# Revit family: НЕВАТОМ_Фильтр панельный FVP, Версия 2
name_source: partatom
category: Арматура воздуховодов
revit_build: Autodesk Revit 2017 (Build: 20170118_1100(x64)
units: mm (PartAtom-declared; Revit-internal decimal feet)

## family parameters
Всегда вертикально = Нет
На основе рабочей плоскости = Нет
Общий = Нет
При загрузке вырезать с полостями = Нет
Размер круглого соединителя = Использовать диаметр
Тип детали = Вставляется

## types (8) — shared parameters
ADSK_Единица измерения = шт
ADSK_Завод-изготовитель = НЕВАТОМ
ADSK_Количество = 1
ADSK_Материал = Оцинкованная сталь
ADSK_Материал наименование = Оцинкованная сталь
L = 25 мм
Nevatom_URL = https://t.me
t = 25 мм
zero-valued in all types: ADSK_Масса

## per-type parameters (varying)
| type | ADSK_Расход воздуха |
| 500х500х25 | 1700.0 м³/ч |
| 592х592х25 | 2400.0 м³/ч |
| 592х287х25 | 1200.0 м³/ч |
| 592х490х25 | 2000.0 м³/ч |
| 287х490х25 | 1000.0 м³/ч |
| 610х610х25 | 2600.0 м³/ч |
| 305х305х25 | 650.0 м³/ч |
| 892х287х25 | 1800.0 м³/ч |
